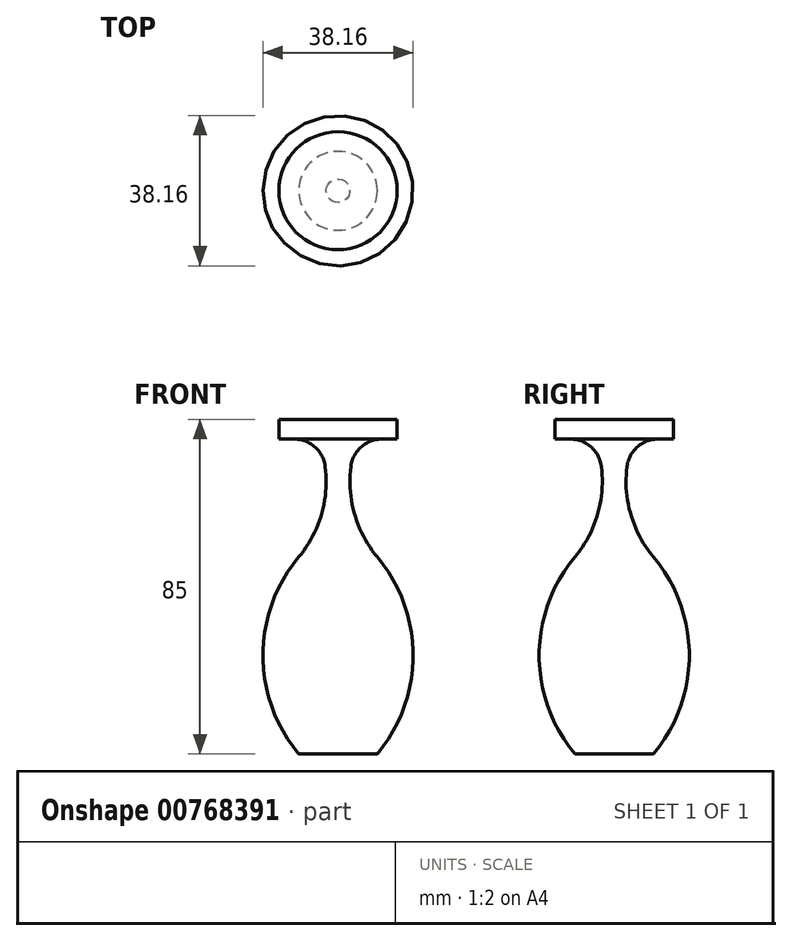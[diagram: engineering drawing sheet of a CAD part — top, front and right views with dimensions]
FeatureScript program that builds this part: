
annotation { "Feature Type Name" : "Feature", "Feature Type Description" : "" }
export const myFeature = defineFeature(function(context is Context, id is Id, definition is map)
    precondition{}
    {
        {
            var Q0;
            Q0=qCreatedBy(makeId("Front.planeOp"),FACE);
            var sketch = newSketch(context, id + "F0", { "sketchPlane" : qUnion([Q0])});
            skLineSegment(sketch, "E0", {"start": v(0, 0) * mm, "end": v(0, 80) * mm});
            skLineSegment(sketch, "E1", {"start": v(0, 0) * mm, "end": v(10, 0) * mm});
            skArc(sketch, "E2", {"start": v(10, 0) * mm, "mid": v(19.08, 25) * mm, "end": v(10, 50) * mm});
            skArc(sketch, "E3", {"start": v(5, 80) * mm, "mid": v(3.42, 64.32) * mm, "end": v(10, 50) * mm});
            skLineSegment(sketch, "E4", {"start": v(15, 80) * mm, "end": v(15, 85) * mm});
            skLineSegment(sketch, "E5", {"start": v(15, 85) * mm, "end": v(0, 85) * mm});
            skLineSegment(sketch, "E6", {"start": v(0, 85) * mm, "end": v(0, 80) * mm});
            skLineSegment(sketch, "E7", {"start": v(15, 80) * mm, "end": v(5, 80) * mm});
            skSolve(sketch);
        }
        {
            var Q0;
            Q0=qSketchRegion(id+"F0",true);
            var Q1;
            Q1=sQuery(id+"F0.wireOp",EDGE,"E0");
            revolve(context, id + "F1", {"entities" : qUnion([Q0]), "axis" : qUnion([Q1]), "revolveType" : RevolveType.FULL});
        }
        {
            var Q0;
            Q0=makeQuery(id+"F1.opRevolve","SWEPT_EDGE",EDGE,{"disambiguationData":[OSD([sQuery(id+"F0.wireOp",EDGE,"E3"),sQuery(id+"F0.wireOp",EDGE,"tCd9H1ch-hhov-lTIr-XZBm-AJwywnV3BYZo")])]});
            fillet(context, id + "F2", {"entities" : qUnion([Q0]), "radius" : 8 * mm, "tangentPropagation" : true, "allowEdgeOverflow" : false});
        }
    });
